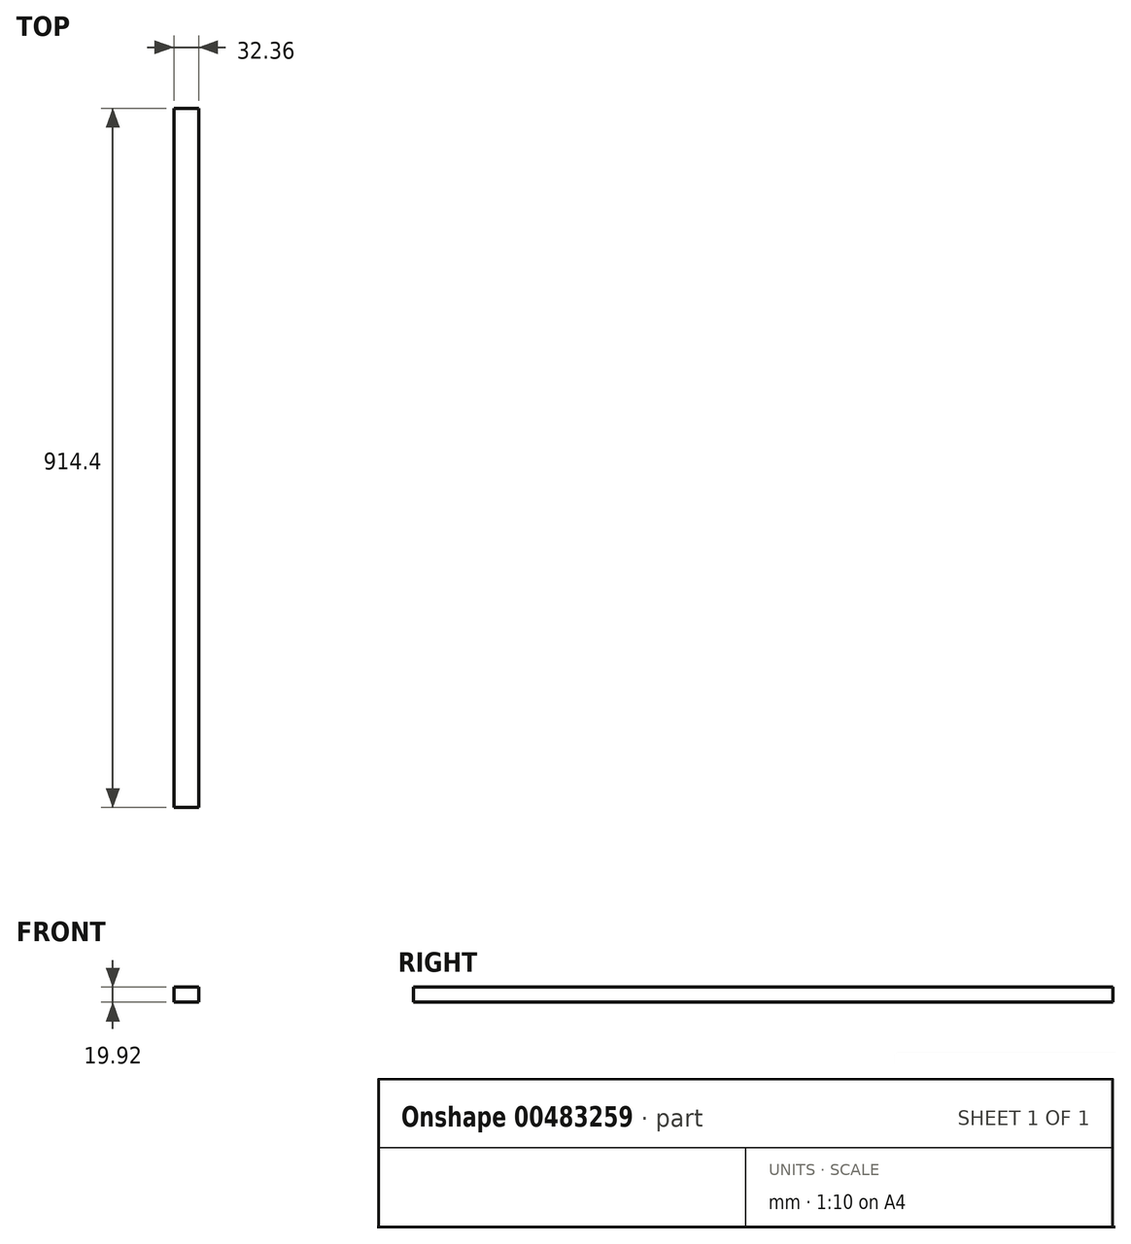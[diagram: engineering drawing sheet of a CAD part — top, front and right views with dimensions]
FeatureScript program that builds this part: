
annotation { "Feature Type Name" : "Feature", "Feature Type Description" : "" }
export const myFeature = defineFeature(function(context is Context, id is Id, definition is map)
    precondition{}
    {
        {
            var Q0;
            Q0=qCreatedBy(makeId("Front.planeOp"),FACE);
            var sketch = newSketch(context, id + "F0", { "sketchPlane" : qUnion([Q0])});
            skLineSegment(sketch, "E0.bottom", {"start": v(0, 17.84) * mm, "end": v(-32.36, 17.84) * mm});
            skLineSegment(sketch, "E0.top", {"start": v(0, 37.76) * mm, "end": v(-32.36, 37.76) * mm});
            skLineSegment(sketch, "E0.left", {"start": v(0, 17.84) * mm, "end": v(0, 37.76) * mm});
            skLineSegment(sketch, "E0.right", {"start": v(-32.36, 17.84) * mm, "end": v(-32.36, 37.76) * mm});
            skPoint(sketch, "E0.middle", {"position": v(-16.18, 27.8) * mm});
            skSolve(sketch);
        }
        {
            var Q0;
            Q0=makeQuery(id+"F0.imprint","IMPRINT",FACE,{"disambiguationData":[TD([[makeQuery(id+"F0.imprint","IMPRINT",EDGE,{"derivedFrom":sQuery(id+"F0.wireOp",EDGE,"E0.bottom")}),-1.0]])]});
            var Q1;
            Q1 = qSketchRegion(id + "F0", true);
            extrude(context, id + "F1", {"entities" : qUnion([Q0, Q1]), "depth" : 914.4 * mm});
        }
    });
